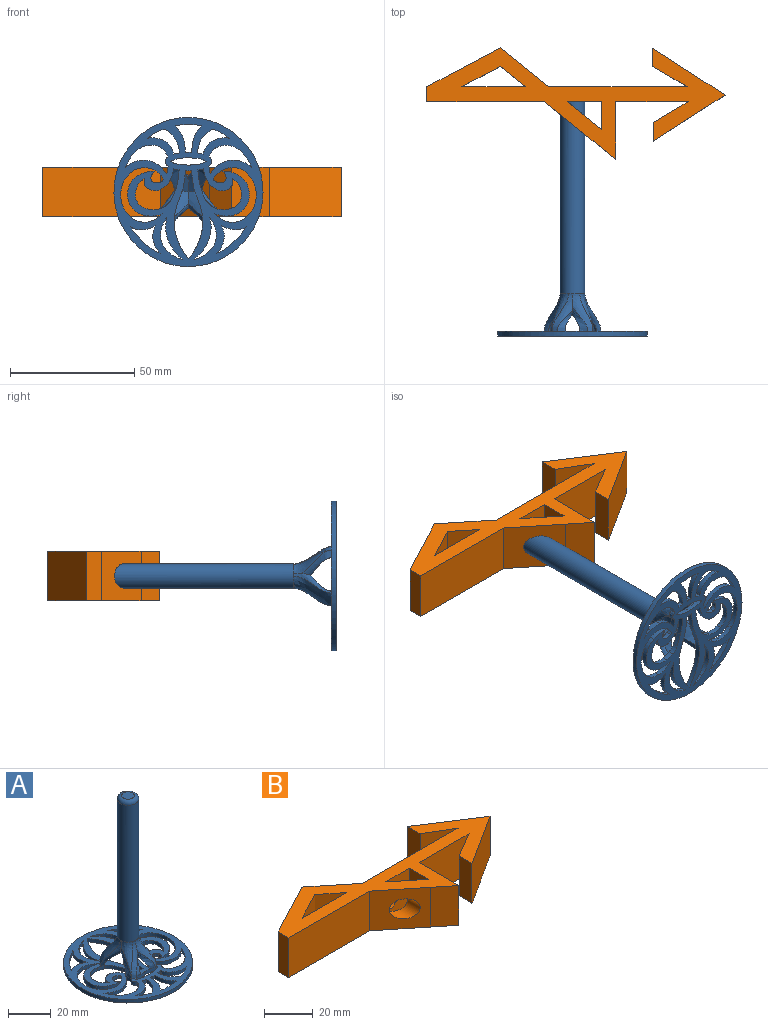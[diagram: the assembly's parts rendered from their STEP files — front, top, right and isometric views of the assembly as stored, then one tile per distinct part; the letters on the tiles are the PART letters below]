
ASSEMBLY  parts=2 mates=1
PART A: 133 faces, bbox 60.1x60.1x97.1 mm
  f0: plane 60.08x60.08mm, normal (0,0,1), area 1509.5mm2, adj f1,f3,f4,f5,f6,f7,f8,f9
  f1: bspline ~15x11.94mm, area 135.3mm2, adj f0,f2,f114,f129,f130
  f2: bspline ~15x11.75mm, area 42.4mm2, adj f1,f42,f113,f119,f122,f123,f130
  f3: extruded ~2x1.32mm, area 2.6mm2, adj f0,f4,f111,f112
  f4: extruded ~2x1.18mm, area 2.4mm2, adj f0,f3,f5,f112
  f5: extruded ~10.65x4.02mm, area 23.4mm2, adj f0,f4,f6,f112
  f6: extruded ~5.27x2mm, area 10.6mm2, adj f0,f5,f7,f112
  f7: extruded ~5.27x2mm, area 10.6mm2, adj f0,f6,f111,f112
  f8: extruded ~10.74x2.55mm, area 22.9mm2, adj f0,f9,f96,f112
  f9: extruded ~16.77x6.84mm, area 37.9mm2, adj f0,f8,f10,f112
  f10: extruded ~4.95x2.26mm, area 11mm2, adj f0,f9,f96,f112
  f11: extruded ~16.77x6.84mm, area 37.9mm2, adj f0,f12,f98,f112
  f12: extruded ~10.74x2.55mm, area 22.9mm2, adj f0,f11,f13,f112
  f13: extruded ~3.77x3.12mm, area 9.9mm2, adj f0,f12,f98,f112
  f14: extruded ~13.36x5.5mm, area 30.9mm2, adj f0,f15,f99,f112
  f15: extruded ~3.38x2.33mm, area 8.3mm2, adj f0,f14,f16,f112
  f16: extruded ~7.97x6mm, area 20.3mm2, adj f0,f15,f17,f112
  f17: extruded ~11.1x4.71mm, area 27mm2, adj f0,f16,f18,f112
  f18: extruded ~3.69x2mm, area 8.7mm2, adj f0,f17,f99,f112,f128
  f19: extruded ~9.96x2mm, area 21mm2, adj f0,f20,f100,f112
  f20: extruded ~11.18x2.93mm, area 24.2mm2, adj f0,f19,f100,f112
  f21: plane 2x0.01mm, normal (0.96,-0.3,0), area 0mm2, adj f0,f22,f101,f112
  f22: extruded ~10.43x5.82mm, area 26.1mm2, adj f0,f21,f23,f112
  f23: extruded ~6.77x3.63mm, area 15.4mm2, adj f0,f22,f24,f112
  f24: extruded ~9.56x6.19mm, area 23.9mm2, adj f0,f23,f25,f112
  f25: extruded ~2.39x2mm, area 4.9mm2, adj f0,f24,f101,f112
  f26: extruded ~3.22x2mm, area 6.9mm2, adj f0,f27,f102,f112
  f27: extruded ~5.08x2mm, area 11.1mm2, adj f0,f26,f28,f112
  f28: extruded ~8.39x5.96mm, area 21.7mm2, adj f0,f27,f29,f112
  f29: extruded ~2x0.26mm, area 0.5mm2, adj f0,f28,f30,f112
  f30: extruded ~2.25x2mm, area 4.6mm2, adj f0,f29,f31,f112
  f31: extruded ~12.22x3.27mm, area 25.5mm2, adj f0,f30,f32,f112
  f32: extruded ~4.78x3.52mm, area 12.2mm2, adj f0,f31,f33,f112,f117
  f33: extruded ~6.03x2mm, area 12.3mm2, adj f0,f32,f34,f112
  f34: extruded ~8.79x3.54mm, area 20.7mm2, adj f0,f33,f102,f112
  f35: extruded ~5.99x5.4mm, area 16.8mm2, adj f0,f36,f103,f112
  f36: extruded ~4.24x2mm, area 8.8mm2, adj f0,f35,f37,f112
  f37: extruded ~3.97x2mm, area 9.1mm2, adj f0,f36,f38,f112
  f38: extruded ~2x0.58mm, area 1.3mm2, adj f0,f37,f39,f112
  f39: extruded ~3.37x2.6mm, area 8.7mm2, adj f0,f38,f40,f112
  f40: extruded ~4.46x2mm, area 9.1mm2, adj f0,f39,f41,f112
  f41: extruded ~8.2x4.3mm, area 20mm2, adj f0,f40,f42,f112
  f42: extruded ~3.5x2mm, area 7.5mm2, adj f0,f2,f41,f43,f112
  f43: extruded ~2.69x2.49mm, area 7.4mm2, adj f0,f42,f44,f112
  f44: extruded ~4.64x2mm, area 10.1mm2, adj f0,f43,f45,f112
  f45: extruded ~7.43x2mm, area 15.1mm2, adj f0,f44,f46,f112
  f46: extruded ~2.25x2mm, area 4.6mm2, adj f0,f45,f103,f112
  f47: extruded ~10.42x5.83mm, area 26.1mm2, adj f0,f48,f104,f112
  f48: extruded ~2x0.74mm, area 1.5mm2, adj f0,f47,f49,f112
  f49: extruded ~2.39x2mm, area 4.9mm2, adj f0,f48,f50,f112
  f50: extruded ~5.81x2mm, area 12.3mm2, adj f0,f49,f51,f112
  f51: extruded ~4.34x3.75mm, area 11.6mm2, adj f0,f50,f104,f112
  f52: extruded ~7x2mm, area 14.5mm2, adj f0,f53,f105,f112
  f53: extruded ~7.13x2mm, area 14.8mm2, adj f0,f52,f54,f112
  f54: extruded ~7x2mm, area 14.5mm2, adj f0,f53,f105,f112,f121
  f55: extruded ~11.18x2.93mm, area 24.2mm2, adj f0,f56,f106,f112
  f56: extruded ~9.96x2mm, area 21mm2, adj f0,f55,f106,f112
  f57: extruded ~7.6x2.62mm, area 16.1mm2, adj f0,f58,f107,f112
  f58: extruded ~20.91x5.77mm, area 44.8mm2, adj f0,f57,f59,f112,f114
  f59: extruded ~20.91x5.77mm, area 44.8mm2, adj f0,f58,f60,f112,f115
  f60: extruded ~7.6x2.62mm, area 16.1mm2, adj f0,f59,f61,f112
  f61: extruded ~7x2mm, area 14.3mm2, adj f0,f60,f62,f112
  f62: extruded ~2.49x2mm, area 5mm2, adj f0,f61,f63,f112
  f63: extruded ~2x0.04mm, area 0.1mm2, adj f0,f62,f107,f112
  f64: extruded ~6.29x2.59mm, area 14mm2, adj f0,f65,f108,f112
  f65: extruded ~7.71x4.71mm, area 18.8mm2, adj f0,f64,f66,f112
  f66: extruded ~2x0.84mm, area 2.3mm2, adj f0,f65,f67,f112
  f67: extruded ~3.16x2mm, area 6.6mm2, adj f0,f66,f68,f112
  f68: extruded ~2x1.3mm, area 3.7mm2, adj f0,f67,f69,f112
  f69: extruded ~3.28x2mm, area 7.5mm2, adj f0,f68,f70,f112
  f70: extruded ~6.39x2mm, area 13.3mm2, adj f0,f69,f71,f112
  f71: extruded ~3.74x3.48mm, area 10.4mm2, adj f0,f70,f72,f112
  f72: extruded ~9.02x2mm, area 18.9mm2, adj f0,f71,f73,f112
  f73: extruded ~12.36x3.74mm, area 27.3mm2, adj f0,f72,f74,f112
  f74: extruded ~6.86x3.39mm, area 15.8mm2, adj f0,f73,f75,f112
  f75: extruded ~6.41x2.62mm, area 14.2mm2, adj f0,f74,f76,f112
  f76: extruded ~8.44x3.38mm, area 18.7mm2, adj f0,f75,f108,f112
  f77: extruded ~3.69x2mm, area 8.8mm2, adj f0,f78,f109,f112,f119
  f78: extruded ~5.02x4.62mm, area 14.4mm2, adj f0,f77,f79,f112
  f79: extruded ~12.08x9.16mm, area 32.9mm2, adj f0,f78,f80,f112
  f80: extruded ~3.38x2.33mm, area 8.3mm2, adj f0,f79,f81,f112
  f81: extruded ~5.5x2mm, area 11.2mm2, adj f0,f80,f82,f112
  f82: extruded ~7.86x5.41mm, area 19.7mm2, adj f0,f81,f109,f112
  f83: extruded ~7.71x4.71mm, area 18.8mm2, adj f0,f84,f110,f112
  f84: extruded ~6.29x2.58mm, area 14mm2, adj f0,f83,f85,f112
  f85: extruded ~8.36x3.4mm, area 18.5mm2, adj f0,f84,f86,f112
  f86: extruded ~8.44x3.38mm, area 18.7mm2, adj f0,f85,f87,f112
  f87: extruded ~6.41x2.62mm, area 14.2mm2, adj f0,f86,f88,f112
  f88: extruded ~6.86x3.39mm, area 15.8mm2, adj f0,f87,f89,f112
  f89: extruded ~12.36x3.74mm, area 27.3mm2, adj f0,f88,f90,f112
  f90: extruded ~9.02x2mm, area 18.9mm2, adj f0,f89,f91,f112
  f91: extruded ~3.74x3.48mm, area 10.4mm2, adj f0,f90,f92,f112
  f92: extruded ~6.39x2mm, area 13.3mm2, adj f0,f91,f93,f112
  f93: extruded ~3.28x2mm, area 7.5mm2, adj f0,f92,f94,f112
  f94: extruded ~2x1.3mm, area 3.7mm2, adj f0,f93,f95,f112
  f95: extruded ~3.16x2mm, area 6.6mm2, adj f0,f94,f110,f112
  f96: extruded ~3.77x3.12mm, area 9.9mm2, adj f0,f8,f10,f112
  f97: extruded ~60x60mm, area 376.2mm2, adj f0,f112
  f98: extruded ~4.95x2.26mm, area 11mm2, adj f0,f11,f13,f112
  f99: extruded ~3.05x2mm, area 6.2mm2, adj f14,f18,f112,f127
  f100: extruded ~11.85x10.8mm, area 32.5mm2, adj f0,f19,f20,f112
  f101: extruded ~2x0.75mm, area 1.5mm2, adj f0,f21,f25,f112
  f102: extruded ~2.91x2.9mm, area 8.4mm2, adj f0,f26,f34,f112
  f103: extruded ~2.66x2mm, area 5.5mm2, adj f0,f35,f46,f112
  f104: extruded ~6.76x3.63mm, area 15.4mm2, adj f0,f47,f51,f112
  f105: extruded ~7.14x2mm, area 14.8mm2, adj f0,f52,f54,f112,f125
  f106: extruded ~11.85x10.8mm, area 32.5mm2, adj f0,f55,f56,f112
  f107: extruded ~6.96x2mm, area 14.1mm2, adj f0,f57,f63,f112
  f108: extruded ~8.36x3.4mm, area 18.5mm2, adj f0,f64,f76,f112
  f109: extruded ~3.05x2mm, area 6.2mm2, adj f0,f77,f82,f112,f123
  f110: extruded ~2x0.84mm, area 2.3mm2, adj f0,f83,f95,f112
  f111: extruded ~10.65x4.02mm, area 23.4mm2, adj f0,f3,f7,f112
  f112: plane 60.09x60.09mm, normal (0,0,-1), area 1548mm2, adj f3,f4,f5,f6,f7,f8,f9,f10
  f113: bspline ~11.54x11.43mm, area 82.6mm2, adj f0,f2,f114,f116,f122
  f114: bspline ~15x11.94mm, area 34.6mm2, adj f1,f58,f113,f115,f116
  f115: bspline ~15x11.95mm, area 34.6mm2, adj f59,f114,f116,f118
  f116: bspline ~11.54x11.44mm, area 81mm2, adj f0,f113,f114,f115,f117,f122,f124,f127
  f117: bspline ~15x11.74mm, area 43.5mm2, adj f32,f116,f118,f127,f128,f130
  f118: bspline ~15x11.95mm, area 135.4mm2, adj f0,f115,f117,f130
  f119: bspline ~15x10.4mm, area 51.3mm2, adj f2,f77,f120,f123,f130
  f120: bspline ~15x12.29mm, area 48.8mm2, adj f0,f119,f121,f125,f126,f130
  f121: bspline ~15x14.7mm, area 25.2mm2, adj f54,f120,f122,f124,f125
  f122: bspline ~16x15mm, area 87.1mm2, adj f0,f2,f113,f116,f121,f123,f124
  f123: bspline ~15.14x15mm, area 40.6mm2, adj f2,f109,f119,f122
  f124: bspline ~16x15mm, area 85.1mm2, adj f0,f116,f121,f122,f125,f127
  f125: bspline ~9.49x9.48mm, area 28.4mm2, adj f105,f120,f121,f124,f126
  f126: bspline ~15x11.18mm, area 62.1mm2, adj f0,f120,f125,f128,f130
  f127: bspline ~15.39x15mm, area 32.6mm2, adj f99,f116,f117,f124,f128
  f128: bspline ~15x11.94mm, area 44.1mm2, adj f18,f117,f126,f127,f130
  f129: bspline ~15.57x15mm, area 0mm2, adj f1,f130
  f130: cylinder r=5mm len=78mm, axis (0,0,-1), area 2450.4mm2, adj f1,f2,f117,f118,f119,f120,f126,f128
  f131: plane 6x6mm, normal (0,0,1), area 28.3mm2, adj f132
  f132: torus R=3mm, axis (0,0,1), area 84.4mm2, adj f130,f131
PART B: 26 faces, bbox 121.7x46.6x21.7 mm
  f0: plane 29.16x20mm, normal (0.54,0.84,0), area 694.5mm2, adj f1,f21,f22,f23
  f1: plane 20x7.29mm, normal (-1,0,0), area 145.8mm2, adj f0,f2,f22,f23
  f2: plane 20x13.9mm, normal (-0.51,-0.86,0), area 322.9mm2, adj f1,f3,f22,f23
  f3: plane 55.66x20mm, normal (0,1,0), area 1113.2mm2, adj f2,f4,f22,f23
  f4: plane 20x19.47mm, normal (0.63,0.78,0), area 500.2mm2, adj f3,f5,f22,f23
  f5: plane 29.6x20mm, normal (-0.47,0.88,0), area 670.1mm2, adj f4,f6,f22,f23
  f6: plane 20x6.05mm, normal (-1,0,0), area 121mm2, adj f5,f7,f22,f23
  f7: plane 47.25x20mm, normal (0,-1,0), area 945mm2, adj f6,f8,f22,f23
  f8: plane 21.69x21.28mm, normal (-0.63,-0.78,0), area 402.1mm2, adj f7,f9,f22,f23,f24
  f9: plane 20x9.19mm, normal (-0.63,-0.78,0), area 236.2mm2, adj f8,f10,f22,f23
  f10: plane 20x7.41mm, normal (1,0,0), area 148.1mm2, adj f9,f11,f22,f23
  f11: plane 20x15.77mm, normal (1,0,0), area 315.5mm2, adj f10,f12,f22,f23
  f12: plane 29.06x20mm, normal (0,-1,0), area 581.2mm2, adj f11,f13,f22,f23
  f13: plane 20x14.07mm, normal (-0.51,0.86,0), area 326.9mm2, adj f12,f14,f22,f23
  f14: plane 20x7.45mm, normal (-1,0,0), area 149mm2, adj f13,f21,f22,f23
  f15: plane 20x11.22mm, normal (-1,0,0), area 224.4mm2, adj f16,f19,f22,f23
  f16: plane 20.04x13.95mm, normal (0.63,0.78,0), area 281.3mm2, adj f15,f19,f22,f23,f24
  f17: plane 25.73x20mm, normal (0,1,0), area 514.5mm2, adj f18,f20,f22,f23
  f18: plane 20x15.62mm, normal (0.46,-0.89,0), area 352.8mm2, adj f17,f20,f22,f23
  f19: plane 20x13.9mm, normal (0,-1,0), area 218.7mm2, adj f15,f16,f22,f23,f24
  f20: plane 20x10.11mm, normal (-0.63,-0.78,0), area 260.3mm2, adj f17,f18,f22,f23
  f21: plane 28.95x20mm, normal (0.54,-0.84,0), area 686.9mm2, adj f0,f14,f22,f23
  f22: plane 120x44.92mm, normal (0,0,1), area 1511.9mm2, adj f0,f1,f2,f3,f4,f5,f6,f7
  f23: plane 120x44.92mm, normal (0,0,-1), area 1511.9mm2, adj f0,f1,f2,f3,f4,f5,f6,f7
  f24: cylinder r=5mm len=15.84mm, axis (0,-1,0), area 297mm2, adj f8,f16,f19,f25
  f25: plane 10x10mm, normal (0,-1,0), area 78.5mm2, adj f24
PLACE A rot(axis=(-1,0,0),90deg) t=(0,-97,10)mm
PLACE B at identity
MATE slider A.f130 <-> B.f24  axis (0,1,0) through (0,0,10)mm
